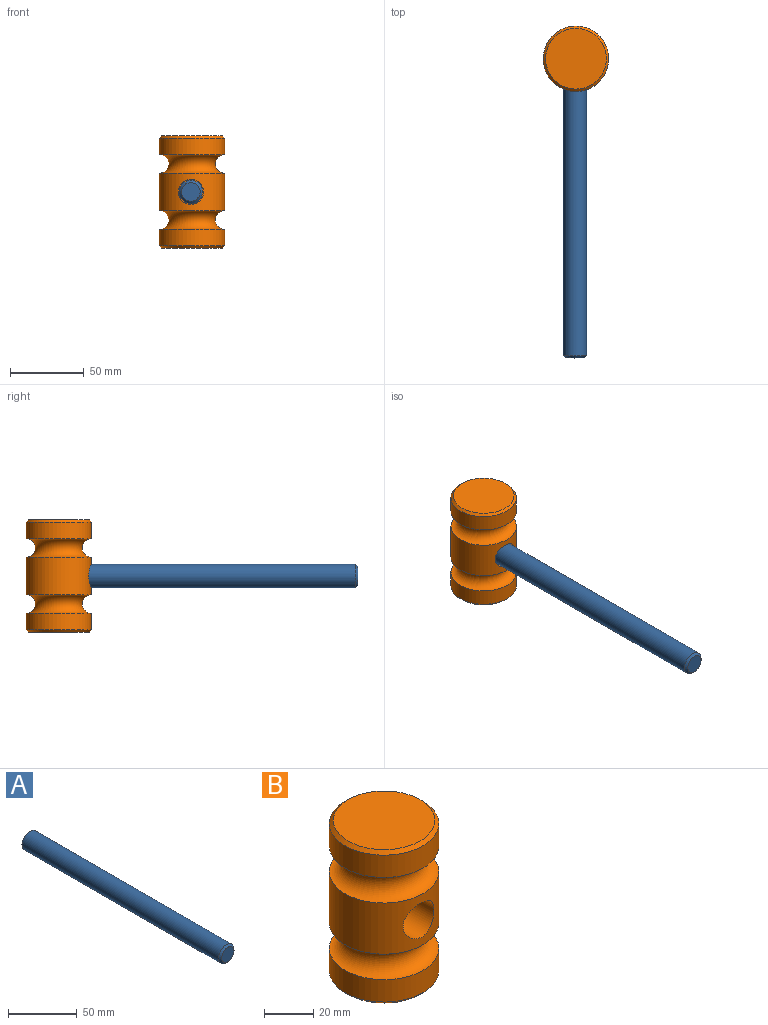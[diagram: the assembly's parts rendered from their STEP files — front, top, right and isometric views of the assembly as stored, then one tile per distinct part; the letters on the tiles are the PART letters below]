
ASSEMBLY  parts=2 mates=1
PART A: 4 faces, bbox 15.9x203.2x15.9 mm
  f0: cylinder r=7.94mm len=201.59mm, axis (0,1,0), area 10053.7mm2, adj f2,f3
  f1: plane 12.65x12.65mm, normal (0,-1,0), area 125.7mm2, adj f3
  f2: plane 15.88x15.88mm, normal (0,1,0), area 197.9mm2, adj f0
  f3: cone r=6.32mm half-angle=45deg, axis (0,1,0), area 102.2mm2, adj f0,f1
PART B: 11 faces, bbox 57.9x57.9x76.2 mm
  f0: plane 41.25x41.25mm, normal (0,0,1), area 1336.4mm2, adj f8
  f1: plane 41.25x41.25mm, normal (0,0,-1), area 1336.4mm2, adj f7
  f2: cylinder r=22.23mm len=44.45mm, axis (0,0,1), area 1550mm2, adj f3,f7
  f3: torus R=22.23mm, axis (0,0,1), area 2279.1mm2, adj f2,f4
  f4: cylinder r=22.23mm len=44.45mm, axis (0,0,1), area 3311.9mm2, adj f3,f5,f9
  f5: torus R=22.23mm, axis (0,0,1), area 2279.1mm2, adj f4,f6
  f6: cylinder r=22.23mm len=44.45mm, axis (0,0,1), area 1550mm2, adj f5,f8
  f7: cone r=22.23mm half-angle=45deg, axis (0,0,1), area 304.6mm2, adj f1,f2
  f8: cone r=20.62mm half-angle=45deg, axis (0,0,-1), area 304.6mm2, adj f0,f6
  f9: cylinder r=8.57mm len=22.23mm, axis (0,-1,0), area 1150.6mm2, adj f4,f10
  f10: plane 17.15x17.15mm, normal (0,-1,0), area 230.9mm2, adj f9
PLACE A t=(-30.81,-25.21,-6.56)mm
PLACE B t=(-25.73,-25.21,13.95)mm
MATE fastened A.f0 <-> B.f9  axis (0,1,0) through (-76.75,-25.21,28.08)mm
